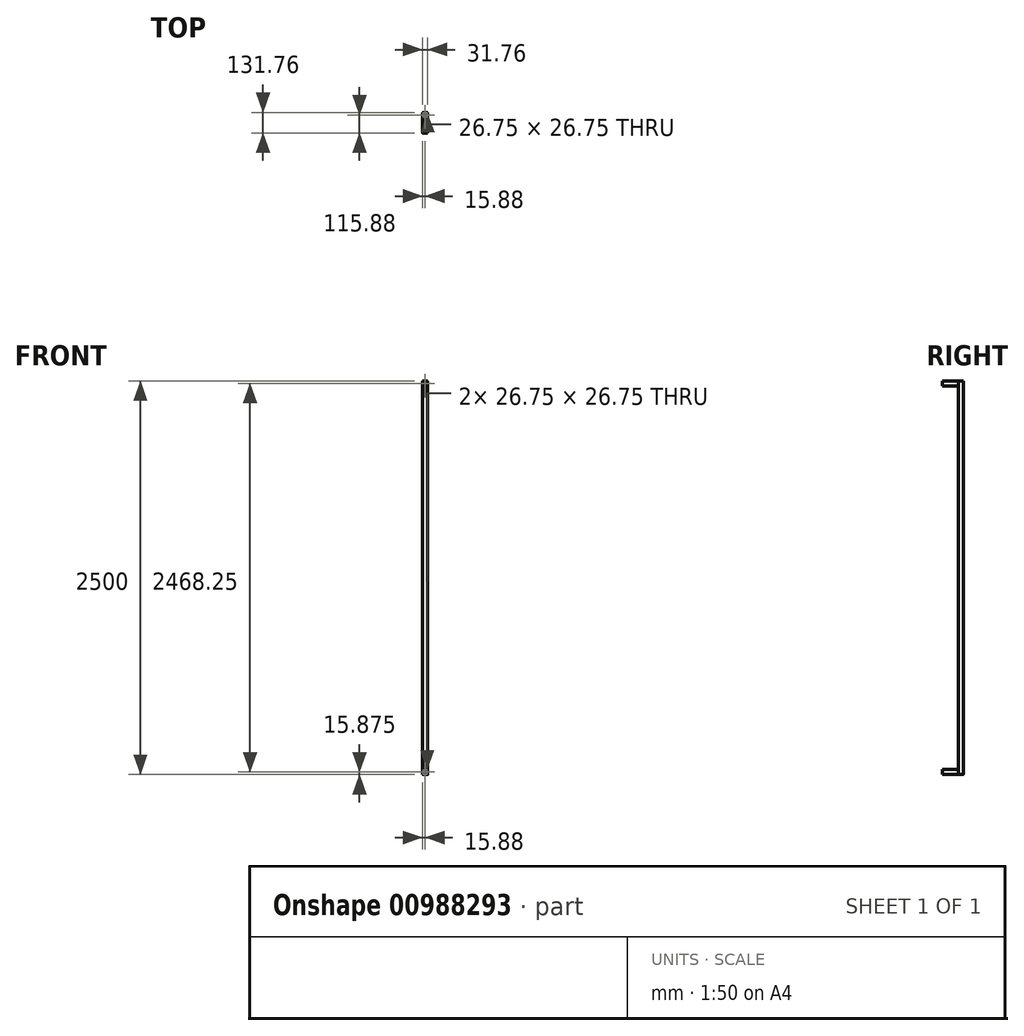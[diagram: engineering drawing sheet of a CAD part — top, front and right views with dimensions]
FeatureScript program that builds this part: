
annotation { "Feature Type Name" : "Feature", "Feature Type Description" : "" }
export const myFeature = defineFeature(function(context is Context, id is Id, definition is map)
    precondition{}
    {
        {
            var Q0;
            Q0=qCreatedBy(makeId("Top.planeOp"),FACE);
            var sketch = newSketch(context, id + "F0", { "sketchPlane" : qUnion([Q0])});
            skLineSegment(sketch, "E0.bottom", {"start": v(13.38, 15.88) * mm, "end": v(-13.38, 15.88) * mm});
            skLineSegment(sketch, "E0.top", {"start": v(13.37, -15.88) * mm, "end": v(-13.37, -15.88) * mm});
            skLineSegment(sketch, "E0.left", {"start": v(15.88, 13.38) * mm, "end": v(15.88, -13.37) * mm});
            skLineSegment(sketch, "E0.right", {"start": v(-15.88, 13.38) * mm, "end": v(-15.88, -13.37) * mm});
            skPoint(sketch, "E0.middle", {"position": v(0, 0) * mm});
            skPoint(sketch, "E1.visualSharp", {"position": v(-15.88, 15.88) * mm});
            skArc(sketch, "E1.filletArc", {"start": v(-13.38, 15.88) * mm, "mid": v(-15.14, 15.14) * mm, "end": v(-15.88, 13.38) * mm});
            skPoint(sketch, "E2.visualSharp", {"position": v(15.88, 15.88) * mm});
            skArc(sketch, "E2.filletArc", {"start": v(15.88, 13.38) * mm, "mid": v(15.14, 15.14) * mm, "end": v(13.38, 15.88) * mm});
            skPoint(sketch, "E3.visualSharp", {"position": v(15.88, -15.88) * mm});
            skArc(sketch, "E3.filletArc", {"start": v(13.37, -15.88) * mm, "mid": v(15.14, -15.14) * mm, "end": v(15.88, -13.37) * mm});
            skPoint(sketch, "E4.visualSharp", {"position": v(-15.88, -15.88) * mm});
            skArc(sketch, "E4.filletArc", {"start": v(-15.88, -13.37) * mm, "mid": v(-15.14, -15.14) * mm, "end": v(-13.37, -15.88) * mm});
            skLineSegment(sketch, "E5.0", {"start": v(13.38, 13.38) * mm, "end": v(13.38, 13.38) * mm});
            skLineSegment(sketch, "E5.1", {"start": v(13.38, 13.38) * mm, "end": v(13.38, -13.38) * mm});
            skLineSegment(sketch, "E5.2", {"start": v(13.38, 13.38) * mm, "end": v(-13.37, 13.38) * mm});
            skLineSegment(sketch, "E5.3", {"start": v(13.37, -13.37) * mm, "end": v(13.37, -13.37) * mm});
            skLineSegment(sketch, "E5.4", {"start": v(-13.37, 13.37) * mm, "end": v(-13.37, 13.37) * mm});
            skLineSegment(sketch, "E5.5", {"start": v(-13.37, 13.38) * mm, "end": v(-13.37, -13.38) * mm});
            skLineSegment(sketch, "E5.6", {"start": v(-13.37, -13.37) * mm, "end": v(-13.37, -13.37) * mm});
            skLineSegment(sketch, "E5.7", {"start": v(13.38, -13.38) * mm, "end": v(-13.37, -13.38) * mm});
            skSolve(sketch);
        }
        {
            var Q0;
            Q0=makeQuery(id+"F0.imprint","IMPRINT",FACE,{"disambiguationData":[TD([[makeQuery(id+"F0.imprint","IMPRINT",EDGE,{"derivedFrom":sQuery(id+"F0.wireOp",EDGE,"E0.bottom")}),1.0]])]});
            extrude(context, id + "F1", {"entities" : qUnion([Q0]), "depth" : 2500 * mm, "offsetDistance" : 25 * mm});
        }
        {
            var Q0;
            Q0=makeQuery(id+"F1.opExtrude","SWEPT_FACE",FACE,{"disambiguationData":[OSD([sQuery(id+"F0.wireOp",EDGE,"E0.top")])]});
            var sketch = newSketch(context, id + "F2", { "sketchPlane" : qUnion([Q0])});
            skLineSegment(sketch, "E6.bottom", {"start": v(13.38, 2468.25) * mm, "end": v(-13.37, 2468.25) * mm});
            skLineSegment(sketch, "E6.top", {"start": v(13.38, 2500) * mm, "end": v(-13.37, 2500) * mm});
            skLineSegment(sketch, "E6.left", {"start": v(15.88, 2470.75) * mm, "end": v(15.88, 2497.5) * mm});
            skLineSegment(sketch, "E6.right", {"start": v(-15.87, 2470.75) * mm, "end": v(-15.87, 2497.5) * mm});
            skPoint(sketch, "E6.middle", {"position": v(0, 2484.12) * mm});
            skPoint(sketch, "E7.visualSharp", {"position": v(15.88, 2500) * mm});
            skArc(sketch, "E7.filletArc", {"start": v(15.87, 2497.5) * mm, "mid": v(15.14, 2499.27) * mm, "end": v(13.38, 2500) * mm});
            skPoint(sketch, "E8.visualSharp", {"position": v(15.88, 2468.25) * mm});
            skArc(sketch, "E8.filletArc", {"start": v(13.38, 2468.25) * mm, "mid": v(15.14, 2468.98) * mm, "end": v(15.88, 2470.75) * mm});
            skPoint(sketch, "E9.visualSharp", {"position": v(-15.87, 2468.25) * mm});
            skArc(sketch, "E9.filletArc", {"start": v(-15.88, 2470.75) * mm, "mid": v(-15.14, 2468.98) * mm, "end": v(-13.37, 2468.25) * mm});
            skPoint(sketch, "E10.visualSharp", {"position": v(-15.87, 2500) * mm});
            skArc(sketch, "E10.filletArc", {"start": v(-13.37, 2500) * mm, "mid": v(-15.14, 2499.27) * mm, "end": v(-15.88, 2497.5) * mm});
            skLineSegment(sketch, "E11.0", {"start": v(13.38, 2497.5) * mm, "end": v(-13.37, 2497.5) * mm});
            skLineSegment(sketch, "E11.1", {"start": v(13.38, 2470.75) * mm, "end": v(13.38, 2497.5) * mm});
            skLineSegment(sketch, "E11.2", {"start": v(13.38, 2470.75) * mm, "end": v(-13.37, 2470.75) * mm});
            skLineSegment(sketch, "E11.3", {"start": v(-13.37, 2470.75) * mm, "end": v(-13.37, 2497.5) * mm});
            skLineSegment(sketch, "E12.bottom", {"start": v(13.37, 0) * mm, "end": v(-13.37, 0) * mm});
            skLineSegment(sketch, "E12.top", {"start": v(13.37, 31.75) * mm, "end": v(-13.37, 31.75) * mm});
            skLineSegment(sketch, "E12.left", {"start": v(15.87, 2.5) * mm, "end": v(15.87, 29.25) * mm});
            skLineSegment(sketch, "E12.right", {"start": v(-15.88, 2.5) * mm, "end": v(-15.88, 29.25) * mm});
            skPoint(sketch, "E12.middle", {"position": v(0, 15.88) * mm});
            skPoint(sketch, "E13.visualSharp", {"position": v(15.87, 31.75) * mm});
            skArc(sketch, "E13.filletArc", {"start": v(15.87, 29.25) * mm, "mid": v(15.14, 31.02) * mm, "end": v(13.37, 31.75) * mm});
            skPoint(sketch, "E14.visualSharp", {"position": v(15.87, 0) * mm});
            skArc(sketch, "E14.filletArc", {"start": v(13.37, 0) * mm, "mid": v(15.14, 0.73) * mm, "end": v(15.87, 2.5) * mm});
            skPoint(sketch, "E15.visualSharp", {"position": v(-15.88, 0) * mm});
            skArc(sketch, "E15.filletArc", {"start": v(-15.88, 2.5) * mm, "mid": v(-15.14, 0.73) * mm, "end": v(-13.37, 0) * mm});
            skPoint(sketch, "E16.visualSharp", {"position": v(-15.88, 31.75) * mm});
            skArc(sketch, "E16.filletArc", {"start": v(-13.37, 31.75) * mm, "mid": v(-15.14, 31.02) * mm, "end": v(-15.88, 29.25) * mm});
            skLineSegment(sketch, "E17.0", {"start": v(13.37, 29.25) * mm, "end": v(-13.38, 29.25) * mm});
            skLineSegment(sketch, "E17.1", {"start": v(13.37, 2.5) * mm, "end": v(13.37, 29.25) * mm});
            skLineSegment(sketch, "E17.2", {"start": v(13.37, 2.5) * mm, "end": v(-13.38, 2.5) * mm});
            skLineSegment(sketch, "E17.3", {"start": v(-13.38, 2.5) * mm, "end": v(-13.38, 29.25) * mm});
            skSolve(sketch);
        }
        {
            var Q0;
            Q0=qSketchRegion(id+"F2",true);
            extrude(context, id + "F3", {"entities" : qUnion([Q0]), "surfaceOperationType" : NewSurfaceOperationType.ADD, "depth" : 100 * mm, "offsetDistance" : 25 * mm});
        }
    });
